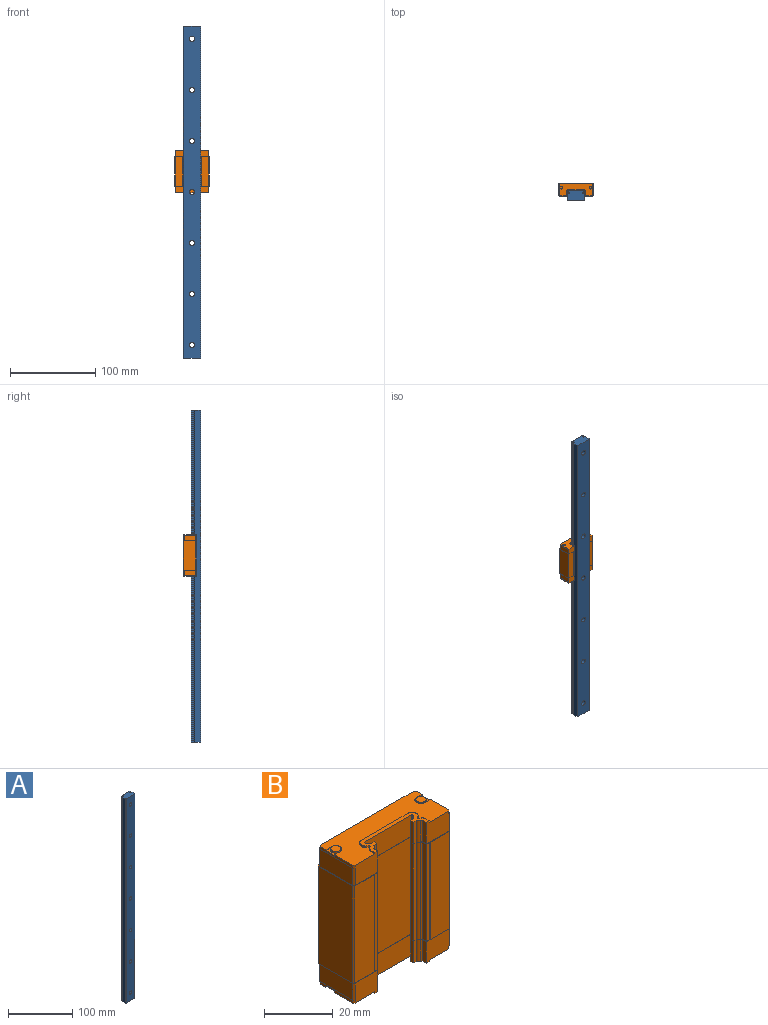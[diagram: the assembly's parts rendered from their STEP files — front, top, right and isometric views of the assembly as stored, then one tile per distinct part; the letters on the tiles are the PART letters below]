
ASSEMBLY  parts=2 mates=1
PART A: 47 faces, bbox 20x11x390 mm
  f0: plane 390x0.3mm, normal (-0.71,0.71,0), area 165.5mm2, adj f1,f2,f3,f27
  f1: plane 20x11mm, normal (0,0,1), area 210.1mm2, adj f0,f2,f3,f4,f5,f6,f7,f8
  f2: plane 390x19.4mm, normal (0,1,0), area 7069.8mm2, adj f0,f1,f24,f25,f27,f29,f32,f35
  f3: plane 390x0.48mm, normal (-1,0,0), area 185.7mm2, adj f0,f1,f4,f27
  f4: plane 390x0.56mm, normal (-0.5,-0.87,0), area 252.2mm2, adj f1,f3,f5,f27
  f5: cylinder r=1.75mm len=390mm, axis (0,0,1), area 427.5mm2, adj f1,f4,f6,f27
  f6: plane 390x1.22mm, normal (0,-1,0), area 474.9mm2, adj f1,f5,f7,f27
  f7: plane 390x1.2mm, normal (-1,0,0), area 468mm2, adj f1,f6,f8,f27
  f8: plane 390x1.22mm, normal (0,1,0), area 474.9mm2, adj f1,f7,f9,f27
  f9: cylinder r=1.75mm len=390mm, axis (0,0,1), area 427.5mm2, adj f1,f8,f10,f27
  f10: plane 390x0.56mm, normal (-0.5,0.87,0), area 252.2mm2, adj f1,f9,f11,f27
  f11: plane 390x6.28mm, normal (-1,0,0), area 2447.7mm2, adj f1,f10,f12,f27
  f12: plane 390x0.5mm, normal (-0.71,-0.71,0), area 275.8mm2, adj f1,f11,f13,f27
  f13: plane 390x19mm, normal (0,-1,0), area 7212.1mm2, adj f1,f12,f14,f27,f28,f31,f34,f37
  f14: plane 390x0.5mm, normal (0.71,-0.71,0), area 275.8mm2, adj f1,f13,f15,f27
  f15: plane 390x6.28mm, normal (1,0,0), area 2447.7mm2, adj f1,f14,f16,f27
  f16: plane 390x0.56mm, normal (0.5,0.87,0), area 252.2mm2, adj f1,f15,f17,f27
  f17: cylinder r=1.75mm len=390mm, axis (0,0,1), area 427.5mm2, adj f1,f16,f18,f27
  f18: plane 390x1.22mm, normal (0,1,0), area 474.9mm2, adj f1,f17,f19,f27
  f19: plane 390x1.2mm, normal (1,0,0), area 468mm2, adj f1,f18,f20,f27
  f20: plane 390x1.22mm, normal (0,-1,0), area 474.9mm2, adj f1,f19,f21,f27
  f21: cylinder r=1.75mm len=390mm, axis (0,0,1), area 427.5mm2, adj f1,f20,f22,f27
  f22: plane 390x0.56mm, normal (0.5,-0.87,0), area 252.2mm2, adj f1,f21,f23,f27
  f23: plane 390x0.48mm, normal (1,0,0), area 185.7mm2, adj f1,f22,f24,f27
  f24: plane 390x0.3mm, normal (0.71,0.71,0), area 165.5mm2, adj f1,f2,f23,f27
  f25: cylinder r=4.75mm len=9.5mm, axis (0,1,0), area 164.1mm2, adj f2,f26
  f26: plane 9.5x9.5mm, normal (0,1,0), area 42.6mm2, adj f25,f28
  f27: plane 20x11mm, normal (0,0,-1), area 210.1mm2, adj f0,f2,f3,f4,f5,f6,f7,f8
  f28: cylinder r=3mm len=6mm, axis (0,1,0), area 103.7mm2, adj f13,f26
  f29: cylinder r=4.75mm len=9.5mm, axis (0,1,0), area 164.1mm2, adj f2,f30
  f30: plane 9.5x9.5mm, normal (0,1,0), area 42.6mm2, adj f29,f31
  f31: cylinder r=3mm len=6mm, axis (0,1,0), area 103.7mm2, adj f13,f30
  f32: cylinder r=4.75mm len=9.5mm, axis (0,1,0), area 164.1mm2, adj f2,f33
  f33: plane 9.5x9.5mm, normal (0,1,0), area 42.6mm2, adj f32,f34
  f34: cylinder r=3mm len=6mm, axis (0,1,0), area 103.7mm2, adj f13,f33
  f35: cylinder r=4.75mm len=9.5mm, axis (0,1,0), area 164.1mm2, adj f2,f36
  f36: plane 9.5x9.5mm, normal (0,1,0), area 42.6mm2, adj f35,f37
  f37: cylinder r=3mm len=6mm, axis (0,1,0), area 103.7mm2, adj f13,f36
  f38: cylinder r=4.75mm len=9.5mm, axis (0,1,0), area 164.1mm2, adj f2,f39
  f39: plane 9.5x9.5mm, normal (0,1,0), area 42.6mm2, adj f38,f40
  f40: cylinder r=3mm len=6mm, axis (0,1,0), area 103.7mm2, adj f13,f39
  f41: cylinder r=4.75mm len=9.5mm, axis (0,1,0), area 164.1mm2, adj f2,f42
  f42: plane 9.5x9.5mm, normal (0,1,0), area 42.6mm2, adj f41,f43
  f43: cylinder r=3mm len=6mm, axis (0,1,0), area 103.7mm2, adj f13,f42
  f44: cylinder r=4.75mm len=9.5mm, axis (0,1,0), area 164.1mm2, adj f2,f45
  f45: plane 9.5x9.5mm, normal (0,1,0), area 42.6mm2, adj f44,f46
  f46: cylinder r=3mm len=6mm, axis (0,1,0), area 103.7mm2, adj f13,f45
PART B: 250 faces, bbox 40x15x50 mm
  f0: cone r=1.62mm half-angle=60deg, axis (0,1,0), area 9.5mm2, adj f107
  f1: plane 1x0.5mm, normal (0.71,-0.71,0), area 0.7mm2, adj f3,f6,f148,f215
  f2: plane 1x0.5mm, normal (-0.71,-0.71,0), area 0.7mm2, adj f9,f143,f148,f215
  f3: plane 7.4x1mm, normal (1,0,0), area 7.4mm2, adj f1,f148,f215,f222
  f4: plane 9.3x7.65mm, normal (0,-1,0), area 67.1mm2, adj f30,f96,f112,f146,f166,f175,f180,f181
  f5: plane 9.3x7.65mm, normal (0,-1,0), area 67.1mm2, adj f13,f29,f96,f146,f166,f174,f180,f197
  f6: plane 9.3x7.65mm, normal (0,-1,0), area 67.1mm2, adj f1,f7,f31,f49,f117,f148,f165,f215
  f7: plane 22.46x7.13mm, normal (0,0,1), area 47mm2, adj f6,f9,f17,f22,f23,f24,f31,f32
  f8: plane 34.6x0.3mm, normal (0.71,-0.71,0), area 14.7mm2, adj f26,f121,f122,f226
  f9: plane 9.3x7.65mm, normal (0,-1,0), area 67.1mm2, adj f2,f7,f32,f49,f118,f148,f149,f215
  f10: plane 34.6x1.68mm, normal (1,0,0), area 58mm2, adj f12,f121,f122,f244
  f11: plane 34.6x1.26mm, normal (0,-1,0), area 43.5mm2, adj f27,f121,f122,f136
  f12: plane 34.6x1.26mm, normal (0,-1,0), area 43.5mm2, adj f10,f121,f122,f137
  f13: plane 6.2x0.5mm, normal (0.71,-0.71,0), area 4.4mm2, adj f5,f73,f96,f109,f122,f166
  f14: plane 34.6x1.22mm, normal (0,1,0), area 42.1mm2, adj f15,f16,f121,f122
  f15: plane 34.6x1.2mm, normal (1,0,0), area 41.5mm2, adj f14,f121,f122,f249
  f16: cylinder r=1.75mm len=34.6mm, axis (0,0,1), area 37.9mm2, adj f14,f25,f121,f122
  f17: plane 7.65x1.22mm, normal (0,1,0), area 9.3mm2, adj f7,f22,f37,f49
  f18: plane 7.65x1.22mm, normal (0,1,0), area 9.3mm2, adj f19,f20,f96,f146
  f19: plane 7.65x1.2mm, normal (1,0,0), area 9.2mm2, adj f18,f96,f146,f248
  f20: cylinder r=1.75mm len=7.65mm, axis (0,0,1), area 8.4mm2, adj f18,f21,f96,f146
  f21: plane 7.65x0.56mm, normal (0.5,0.87,0), area 4.9mm2, adj f20,f28,f96,f146
  f22: cylinder r=1.75mm len=7.65mm, axis (0,0,1), area 8.4mm2, adj f7,f17,f23,f49
  f23: plane 7.65x0.56mm, normal (0.5,0.87,0), area 4.9mm2, adj f7,f22,f24,f49
  f24: plane 7.65x0.48mm, normal (1,0,0), area 3.6mm2, adj f7,f23,f48,f49
  f25: plane 34.6x0.56mm, normal (0.5,0.87,0), area 22.4mm2, adj f16,f26,f121,f122
  f26: plane 34.6x0.48mm, normal (1,0,0), area 16.5mm2, adj f8,f25,f121,f122
  f27: plane 34.6x1.68mm, normal (-1,0,0), area 58mm2, adj f11,f121,f122,f243
  f28: plane 7.65x0.48mm, normal (1,0,0), area 3.6mm2, adj f21,f96,f146,f223
  f29: plane 7.65x1.68mm, normal (-1,0,0), area 12.8mm2, adj f5,f96,f146,f241
  f30: plane 7.65x1.68mm, normal (1,0,0), area 12.8mm2, adj f4,f96,f146,f246
  f31: plane 7.65x1.68mm, normal (-1,0,0), area 12.8mm2, adj f6,f7,f38,f49
  f32: plane 7.65x1.68mm, normal (1,0,0), area 12.8mm2, adj f7,f9,f34,f49
  f33: plane 3x3mm, normal (0,0,-1), area 7.1mm2, adj f212
  f34: plane 7.65x0.56mm, normal (0.5,-0.87,0), area 4.9mm2, adj f7,f32,f35,f49
  f35: cylinder r=1.75mm len=7.65mm, axis (0,0,1), area 8.4mm2, adj f7,f34,f36,f49
  f36: plane 7.65x1.22mm, normal (0,-1,0), area 9.3mm2, adj f7,f35,f37,f49
  f37: plane 7.65x1.2mm, normal (1,0,0), area 9.2mm2, adj f7,f17,f36,f49
  f38: plane 7.65x0.56mm, normal (-0.5,-0.87,0), area 4.9mm2, adj f7,f31,f39,f49
  f39: cylinder r=1.75mm len=7.65mm, axis (0,0,1), area 8.4mm2, adj f7,f38,f40,f49
  f40: plane 7.65x1.22mm, normal (0,-1,0), area 9.3mm2, adj f7,f39,f41,f49
  f41: plane 7.65x1.2mm, normal (-1,0,0), area 9.2mm2, adj f7,f40,f42,f49
  f42: plane 7.65x1.22mm, normal (0,1,0), area 9.3mm2, adj f7,f41,f43,f49
  f43: cylinder r=1.75mm len=7.65mm, axis (0,0,1), area 8.4mm2, adj f7,f42,f44,f49
  f44: plane 7.65x0.56mm, normal (-0.5,0.87,0), area 4.9mm2, adj f7,f43,f45,f49
  f45: plane 7.65x0.48mm, normal (-1,0,0), area 3.6mm2, adj f7,f44,f46,f49
  f46: plane 7.65x0.3mm, normal (-0.71,-0.71,0), area 3.2mm2, adj f7,f45,f47,f49
  f47: plane 19.4x7.65mm, normal (0,-1,0), area 148.4mm2, adj f7,f46,f48,f49
  f48: plane 7.65x0.3mm, normal (0.71,-0.71,0), area 3.2mm2, adj f7,f24,f47,f49
  f49: plane 38.7x5.95mm, normal (0,0,-1), area 2.9mm2, adj f6,f9,f17,f22,f23,f24,f31,f32
  f50: plane 9.3x0.05mm, normal (0,-1,0), area 0.5mm2, adj f49,f51,f117,f121
  f51: plane 1.68x0.05mm, normal (-1,0,0), area 0.1mm2, adj f49,f50,f52,f121
  f52: plane 0.54x0.29mm, normal (-0.48,-0.88,0), area 0mm2, adj f49,f51,f53,f121
  f53: cylinder r=1.7mm len=0.83mm, axis (0,0,1), area 0.1mm2, adj f49,f52,f54,f121
  f54: plane 1.2x0.05mm, normal (0,-1,0), area 0.1mm2, adj f49,f53,f55,f121
  f55: plane 1.1x0.05mm, normal (-1,0,0), area 0.1mm2, adj f49,f54,f56,f121
  f56: plane 1.2x0.05mm, normal (0,1,0), area 0.1mm2, adj f49,f55,f57,f121
  f57: cylinder r=1.7mm len=0.83mm, axis (0,0,1), area 0.1mm2, adj f49,f56,f58,f121
  f58: plane 0.54x0.29mm, normal (-0.48,0.88,0), area 0mm2, adj f49,f57,f59,f121
  f59: plane 0.58x0.05mm, normal (-1,0,0), area 0mm2, adj f49,f58,f60,f121
  f60: plane 0.3x0.3mm, normal (-0.71,-0.71,0), area 0mm2, adj f49,f59,f61,f121
  f61: plane 19.5x0.05mm, normal (0,-1,0), area 1mm2, adj f49,f60,f62,f121
  f62: plane 0.3x0.3mm, normal (0.71,-0.71,0), area 0mm2, adj f49,f61,f63,f121
  f63: plane 0.58x0.05mm, normal (1,0,0), area 0mm2, adj f49,f62,f64,f121
  f64: plane 0.54x0.29mm, normal (0.48,0.88,0), area 0mm2, adj f49,f63,f65,f121
  f65: cylinder r=1.7mm len=0.83mm, axis (0,0,1), area 0.1mm2, adj f49,f64,f66,f121
  f66: plane 1.2x0.05mm, normal (0,1,0), area 0.1mm2, adj f49,f65,f67,f121
  f67: plane 1.1x0.05mm, normal (1,0,0), area 0.1mm2, adj f49,f66,f68,f121
  f68: plane 1.2x0.05mm, normal (0,-1,0), area 0.1mm2, adj f49,f67,f69,f121
  f69: cylinder r=1.7mm len=0.83mm, axis (0,0,1), area 0.1mm2, adj f49,f68,f70,f121
  f70: plane 0.54x0.29mm, normal (0.48,-0.88,0), area 0mm2, adj f49,f69,f71,f121
  f71: plane 1.68x0.05mm, normal (1,0,0), area 0.1mm2, adj f49,f70,f72,f121
  f72: plane 9.3x0.05mm, normal (0,-1,0), area 0.5mm2, adj f49,f71,f118,f121
  f73: plane 9.3x0.05mm, normal (0,-1,0), area 0.5mm2, adj f13,f74,f96,f122
  f74: plane 1.68x0.05mm, normal (-1,0,0), area 0.1mm2, adj f73,f75,f96,f122
  f75: plane 0.54x0.29mm, normal (-0.48,-0.88,0), area 0mm2, adj f74,f76,f96,f122
  f76: cylinder r=1.7mm len=0.83mm, axis (0,0,-1), area 0.1mm2, adj f75,f77,f96,f122
  f77: plane 1.2x0.05mm, normal (0,-1,0), area 0.1mm2, adj f76,f78,f96,f122
  f78: plane 1.1x0.05mm, normal (-1,0,0), area 0.1mm2, adj f77,f79,f96,f122
  f79: plane 1.2x0.05mm, normal (0,1,0), area 0.1mm2, adj f78,f80,f96,f122
  f80: cylinder r=1.7mm len=0.83mm, axis (0,0,-1), area 0.1mm2, adj f79,f81,f96,f122
  f81: plane 0.54x0.29mm, normal (-0.48,0.88,0), area 0mm2, adj f80,f82,f96,f122
  f82: plane 0.58x0.05mm, normal (-1,0,0), area 0mm2, adj f81,f83,f96,f122
  f83: plane 0.3x0.3mm, normal (-0.71,-0.71,0), area 0mm2, adj f82,f84,f96,f122
  f84: plane 19.5x0.05mm, normal (0,-1,0), area 1mm2, adj f83,f85,f96,f122
  f85: plane 0.3x0.3mm, normal (0.71,-0.71,0), area 0mm2, adj f84,f86,f96,f122
  f86: plane 0.58x0.05mm, normal (1,0,0), area 0mm2, adj f85,f87,f96,f122
  f87: plane 0.54x0.29mm, normal (0.48,0.88,0), area 0mm2, adj f86,f88,f96,f122
  f88: cylinder r=1.7mm len=0.83mm, axis (0,0,-1), area 0.1mm2, adj f87,f89,f96,f122
  f89: plane 1.2x0.05mm, normal (0,1,0), area 0.1mm2, adj f88,f90,f96,f122
  f90: plane 1.1x0.05mm, normal (1,0,0), area 0.1mm2, adj f89,f91,f96,f122
  f91: plane 1.2x0.05mm, normal (0,-1,0), area 0.1mm2, adj f90,f92,f96,f122
  f92: cylinder r=1.7mm len=0.83mm, axis (0,0,-1), area 0.1mm2, adj f91,f93,f96,f122
  f93: plane 0.54x0.29mm, normal (0.48,-0.88,0), area 0mm2, adj f92,f94,f96,f122
  f94: plane 1.68x0.05mm, normal (1,0,0), area 0.1mm2, adj f93,f95,f96,f122
  f95: plane 9.3x0.05mm, normal (0,-1,0), area 0.5mm2, adj f94,f96,f112,f122
  f96: plane 38.7x5.95mm, normal (0,0,1), area 2.9mm2, adj f4,f5,f13,f18,f19,f20,f21,f28
  f97: cone r=2mm half-angle=45deg, axis (0,1,0), area 6.1mm2, adj f98,f124
  f98: cylinder r=1.62mm len=7.62mm, axis (0,1,0), area 77.6mm2, adj f97,f99
  f99: cone r=1.62mm half-angle=60deg, axis (0,1,0), area 9.5mm2, adj f98
  f100: cone r=2mm half-angle=45deg, axis (0,1,0), area 6.1mm2, adj f101,f108
  f101: cylinder r=1.62mm len=7.62mm, axis (0,1,0), area 77.6mm2, adj f100,f102
  f102: cone r=1.62mm half-angle=60deg, axis (0,1,0), area 9.5mm2, adj f101
  f103: cone r=2mm half-angle=45deg, axis (0,1,0), area 6.1mm2, adj f104,f124
  f104: cylinder r=1.62mm len=7.62mm, axis (0,1,0), area 77.6mm2, adj f103,f105
  f105: cone r=1.62mm half-angle=60deg, axis (0,1,0), area 9.5mm2, adj f104
  f106: cone r=2mm half-angle=45deg, axis (0,1,0), area 6.1mm2, adj f107,f108
  f107: cylinder r=1.62mm len=7.62mm, axis (0,1,0), area 77.6mm2, adj f0,f106
  f108: plane 34.6x11.7mm, normal (0,1,0), area 379.7mm2, adj f100,f106,f121,f122,f131,f132
  f109: plane 13.4x6.2mm, normal (1,0,0), area 83.1mm2, adj f13,f110,f122,f166
  f110: plane 6.2x0.5mm, normal (0.71,0.71,0), area 4.4mm2, adj f109,f122,f147,f166
  f111: plane 13.4x6.2mm, normal (-1,0,0), area 83.1mm2, adj f112,f113,f122,f166
  f112: plane 6.2x0.5mm, normal (-0.71,-0.71,0), area 4.4mm2, adj f4,f95,f96,f111,f122,f166
  f113: plane 6.2x0.5mm, normal (-0.71,0.71,0), area 4.4mm2, adj f111,f122,f147,f166
  f114: plane 38.6x6.2mm, normal (0,1,0), area 239.3mm2, adj f115,f120,f121,f215
  f115: plane 6.2x0.5mm, normal (0.71,0.71,0), area 4.4mm2, adj f114,f116,f121,f215
  f116: plane 13.4x6.2mm, normal (1,0,0), area 83.1mm2, adj f115,f117,f121,f215
  f117: plane 6.2x0.5mm, normal (0.71,-0.71,0), area 4.4mm2, adj f6,f49,f50,f116,f121,f215
  f118: plane 6.2x0.5mm, normal (-0.71,-0.71,0), area 4.4mm2, adj f9,f49,f72,f119,f121,f215
  f119: plane 13.4x6.2mm, normal (-1,0,0), area 83.1mm2, adj f118,f120,f121,f215
  f120: plane 6.2x0.5mm, normal (-0.71,0.71,0), area 4.4mm2, adj f114,f119,f121,f215
  f121: plane 40x15mm, normal (0,0,1), area 26.7mm2, adj f8,f10,f11,f12,f14,f15,f16,f25
  f122: plane 40x15mm, normal (0,0,-1), area 26.7mm2, adj f8,f10,f11,f12,f13,f14,f15,f16
  f123: plane 34.6x0.5mm, normal (-0.71,0.71,0), area 24.5mm2, adj f121,f122,f124,f140
  f124: plane 34.6x11.7mm, normal (0,1,0), area 379.7mm2, adj f97,f103,f121,f122,f123,f125
  f125: plane 34.6x0.5mm, normal (0.67,0.74,0), area 23.3mm2, adj f121,f122,f124,f126
  f126: plane 34.6x3.6mm, normal (0,1,0), area 124.6mm2, adj f121,f122,f125,f127
  f127: plane 34.6x0.5mm, normal (-0.67,0.74,0), area 23.3mm2, adj f121,f122,f126,f128
  f128: plane 34.6x6.4mm, normal (0,1,0), area 221.4mm2, adj f121,f122,f127,f129
  f129: plane 34.6x0.5mm, normal (0.67,0.74,0), area 23.3mm2, adj f121,f122,f128,f130
  f130: plane 34.6x3.6mm, normal (0,1,0), area 124.6mm2, adj f121,f122,f129,f131
  f131: plane 34.6x0.5mm, normal (-0.67,0.74,0), area 23.3mm2, adj f108,f121,f122,f130
  f132: plane 34.6x0.5mm, normal (0.71,0.71,0), area 24.5mm2, adj f108,f121,f122,f133
  f133: plane 34.6x14mm, normal (1,0,0), area 484.4mm2, adj f121,f122,f132,f134
  f134: plane 34.6x0.5mm, normal (0.71,-0.71,0), area 24.5mm2, adj f121,f122,f133,f135
  f135: plane 34.6x8.03mm, normal (0,-1,0), area 277.8mm2, adj f121,f122,f134,f136
  f136: plane 34.6x0.21mm, normal (-0.42,-0.91,0), area 8.2mm2, adj f11,f121,f122,f135
  f137: plane 34.6x0.21mm, normal (0.42,-0.91,0), area 8.2mm2, adj f12,f121,f122,f138
  f138: plane 34.6x8.03mm, normal (0,-1,0), area 277.8mm2, adj f121,f122,f137,f139
  f139: plane 34.6x0.5mm, normal (-0.71,-0.71,0), area 24.5mm2, adj f121,f122,f138,f140
  f140: plane 34.6x14mm, normal (-1,0,0), area 484.4mm2, adj f121,f122,f123,f139
  f141: plane 2.3x1mm, normal (-1,0,0), area 2.3mm2, adj f145,f148,f215,f216
  f142: cylinder r=1.8mm len=3.6mm, axis (0,0,-1), area 2.3mm2, adj f144,f145,f148,f199
  f143: plane 7.4x1mm, normal (-1,0,0), area 7.4mm2, adj f2,f144,f148,f215
  f144: plane 2.25x1mm, normal (0,1,0), area 1mm2, adj f142,f143,f148,f198,f199,f215
  f145: plane 2.25x1mm, normal (0,-1,0), area 1mm2, adj f141,f142,f148,f198,f199,f215
  f146: plane 22.46x7.13mm, normal (0,0,-1), area 47mm2, adj f4,f5,f18,f19,f20,f21,f28,f29
  f147: plane 38.6x6.2mm, normal (0,1,0), area 239.3mm2, adj f110,f113,f122,f166
  f148: plane 39.5x14.3mm, normal (0,0,1), area 382.6mm2, adj f1,f2,f3,f6,f9,f141,f142,f143
  f149: plane 1.64x0.5mm, normal (-1,0,0), area 0.8mm2, adj f7,f9,f148,f150
  f150: cylinder r=1.3mm len=1.13mm, axis (0,0,-1), area 0.7mm2, adj f7,f148,f149,f151
  f151: plane 0.51x0.5mm, normal (-0.5,0.87,0), area 0.3mm2, adj f7,f148,f150,f152
  f152: cylinder r=0.4mm len=0.69mm, axis (0,0,-1), area 0.4mm2, adj f7,f148,f151,f153
  f153: plane 0.51x0.5mm, normal (-0.5,-0.87,0), area 0.3mm2, adj f7,f148,f152,f154
  f154: cylinder r=1.3mm len=1.13mm, axis (0,0,-1), area 0.7mm2, adj f7,f148,f153,f155
  f155: plane 0.5x0.37mm, normal (-1,0,0), area 0.2mm2, adj f7,f148,f154,f156
  f156: cylinder r=1.6mm len=1.6mm, axis (0,0,-1), area 1.3mm2, adj f7,f148,f155,f157
  f157: plane 19.26x0.5mm, normal (0,1,0), area 9.6mm2, adj f7,f148,f156,f158
  f158: cylinder r=1.6mm len=1.6mm, axis (0,0,-1), area 1.3mm2, adj f7,f148,f157,f159
  f159: plane 0.5x0.37mm, normal (1,0,0), area 0.2mm2, adj f7,f148,f158,f160
  f160: cylinder r=1.3mm len=1.13mm, axis (0,0,-1), area 0.7mm2, adj f7,f148,f159,f161
  f161: plane 0.51x0.5mm, normal (0.5,-0.87,0), area 0.3mm2, adj f7,f148,f160,f162
  f162: cylinder r=0.4mm len=0.69mm, axis (0,0,-1), area 0.4mm2, adj f7,f148,f161,f163
  f163: plane 0.51x0.5mm, normal (0.5,0.87,0), area 0.3mm2, adj f7,f148,f162,f164
  f164: cylinder r=1.3mm len=1.13mm, axis (0,0,-1), area 0.7mm2, adj f7,f148,f163,f165
  f165: plane 1.64x0.5mm, normal (1,0,0), area 0.8mm2, adj f6,f7,f148,f164
  f166: plane 39.6x14.4mm, normal (0,0,-1), area 6.8mm2, adj f4,f5,f13,f109,f110,f111,f112,f113
  f167: plane 1x0.5mm, normal (-0.71,0.71,0), area 0.7mm2, adj f166,f168,f179,f180
  f168: plane 38.5x1mm, normal (0,1,0), area 38.5mm2, adj f166,f167,f169,f180
  f169: plane 1x0.5mm, normal (0.71,0.71,0), area 0.7mm2, adj f166,f168,f170,f180
  f170: plane 2.3x1mm, normal (1,0,0), area 2.3mm2, adj f166,f169,f171,f180
  f171: plane 2.25x1mm, normal (0,-1,0), area 1mm2, adj f166,f170,f180,f204,f205,f213
  f172: plane 2.25x1mm, normal (0,1,0), area 1mm2, adj f166,f173,f180,f204,f205,f213
  f173: plane 7.4x1mm, normal (1,0,0), area 7.4mm2, adj f166,f172,f174,f180
  f174: plane 1x0.5mm, normal (0.71,-0.71,0), area 0.7mm2, adj f5,f166,f173,f180
  f175: plane 1x0.5mm, normal (-0.71,-0.71,0), area 0.7mm2, adj f4,f166,f176,f180
  f176: plane 7.4x1mm, normal (-1,0,0), area 7.4mm2, adj f166,f175,f177,f180
  f177: plane 2.25x1mm, normal (0,1,0), area 1mm2, adj f166,f176,f180,f202,f203,f214
  f178: plane 2.25x1mm, normal (0,-1,0), area 1mm2, adj f166,f179,f180,f202,f203,f214
  f179: plane 2.3x1mm, normal (-1,0,0), area 2.3mm2, adj f166,f167,f178,f180
  f180: plane 39.5x14.3mm, normal (0,0,-1), area 382.6mm2, adj f4,f5,f167,f168,f169,f170,f171,f172
  f181: plane 1.64x0.5mm, normal (-1,0,0), area 0.8mm2, adj f4,f146,f180,f182
  f182: cylinder r=1.3mm len=1.13mm, axis (0,0,1), area 0.7mm2, adj f146,f180,f181,f183
  f183: plane 0.51x0.5mm, normal (-0.5,0.87,0), area 0.3mm2, adj f146,f180,f182,f184
  f184: cylinder r=0.4mm len=0.69mm, axis (0,0,1), area 0.4mm2, adj f146,f180,f183,f185
  f185: plane 0.51x0.5mm, normal (-0.5,-0.87,0), area 0.3mm2, adj f146,f180,f184,f186
  f186: cylinder r=1.3mm len=1.13mm, axis (0,0,1), area 0.7mm2, adj f146,f180,f185,f187
  f187: plane 0.5x0.37mm, normal (-1,0,0), area 0.2mm2, adj f146,f180,f186,f188
  f188: cylinder r=1.6mm len=1.6mm, axis (0,0,1), area 1.3mm2, adj f146,f180,f187,f189
  f189: plane 19.26x0.5mm, normal (0,1,0), area 9.6mm2, adj f146,f180,f188,f190
  f190: cylinder r=1.6mm len=1.6mm, axis (0,0,1), area 1.3mm2, adj f146,f180,f189,f191
  f191: plane 0.5x0.37mm, normal (1,0,0), area 0.2mm2, adj f146,f180,f190,f192
  f192: cylinder r=1.3mm len=1.13mm, axis (0,0,1), area 0.7mm2, adj f146,f180,f191,f193
  f193: plane 0.51x0.5mm, normal (0.5,-0.87,0), area 0.3mm2, adj f146,f180,f192,f194
  f194: cylinder r=0.4mm len=0.69mm, axis (0,0,1), area 0.4mm2, adj f146,f180,f193,f195
  f195: plane 0.51x0.5mm, normal (0.5,0.87,0), area 0.3mm2, adj f146,f180,f194,f196
  f196: cylinder r=1.3mm len=1.13mm, axis (0,0,1), area 0.7mm2, adj f146,f180,f195,f197
  f197: plane 1.64x0.5mm, normal (1,0,0), area 0.8mm2, adj f5,f146,f180,f196
  f198: plane 3.6x0.6mm, normal (-1,0,0), area 2.2mm2, adj f144,f145,f199,f215
  f199: plane 3.85x3.6mm, normal (0,0,1), area 5.4mm2, adj f142,f144,f145,f198,f207
  f200: plane 3.6x0.6mm, normal (1,0,0), area 2.2mm2, adj f201,f215,f220,f222
  f201: plane 3.85x3.6mm, normal (0,0,1), area 5.4mm2, adj f200,f211,f220,f221,f222
  f202: plane 3.6x0.6mm, normal (-1,0,0), area 2.2mm2, adj f166,f177,f178,f203
  f203: plane 3.85x3.6mm, normal (0,0,-1), area 5.4mm2, adj f177,f178,f202,f208,f214
  f204: plane 3.6x0.6mm, normal (1,0,0), area 2.2mm2, adj f166,f171,f172,f205
  f205: plane 3.85x3.6mm, normal (0,0,-1), area 5.4mm2, adj f171,f172,f204,f212,f213
  f206: plane 3x3mm, normal (0,0,1), area 7.1mm2, adj f207
  f207: cylinder r=1.5mm len=3mm, axis (0,0,1), area 5.7mm2, adj f199,f206
  f208: cylinder r=1.5mm len=3mm, axis (0,0,1), area 5.7mm2, adj f203,f209
  f209: plane 3x3mm, normal (0,0,-1), area 7.1mm2, adj f208
  f210: plane 3x3mm, normal (0,0,1), area 7.1mm2, adj f211
  f211: cylinder r=1.5mm len=3mm, axis (0,0,1), area 5.7mm2, adj f201,f210
  f212: cylinder r=1.5mm len=3mm, axis (0,0,1), area 5.7mm2, adj f33,f205
  f213: cylinder r=1.8mm len=3.6mm, axis (0,0,1), area 2.3mm2, adj f171,f172,f180,f205
  f214: cylinder r=1.8mm len=3.6mm, axis (0,0,1), area 2.3mm2, adj f177,f178,f180,f203
  f215: plane 39.6x14.4mm, normal (0,0,1), area 6.8mm2, adj f1,f2,f3,f6,f9,f114,f115,f116
  f216: plane 1x0.5mm, normal (-0.71,0.71,0), area 0.7mm2, adj f141,f148,f215,f217
  f217: plane 38.5x1mm, normal (0,1,0), area 38.5mm2, adj f148,f215,f216,f218
  f218: plane 1x0.5mm, normal (0.71,0.71,0), area 0.7mm2, adj f148,f215,f217,f219
  f219: plane 2.3x1mm, normal (1,0,0), area 2.3mm2, adj f148,f215,f218,f220
  f220: plane 2.25x1mm, normal (0,-1,0), area 1mm2, adj f148,f200,f201,f215,f219,f221
  f221: cylinder r=1.8mm len=3.6mm, axis (0,0,-1), area 2.3mm2, adj f148,f201,f220,f222
  f222: plane 2.25x1mm, normal (0,1,0), area 1mm2, adj f3,f148,f200,f201,f215,f221
  f223: plane 7.65x0.3mm, normal (0.71,-0.71,0), area 3.2mm2, adj f28,f96,f146,f224
  f224: plane 19.4x7.65mm, normal (0,-1,0), area 148.4mm2, adj f96,f146,f223,f225
  f225: plane 7.65x0.3mm, normal (-0.71,-0.71,0), area 3.2mm2, adj f96,f146,f224,f230
  f226: plane 34.6x19.4mm, normal (0,-1,0), area 671.2mm2, adj f8,f121,f122,f227
  f227: plane 34.6x0.3mm, normal (-0.71,-0.71,0), area 14.7mm2, adj f121,f122,f226,f228
  f228: plane 34.6x0.48mm, normal (-1,0,0), area 16.5mm2, adj f121,f122,f227,f229
  f229: plane 34.6x0.56mm, normal (-0.5,0.87,0), area 22.4mm2, adj f121,f122,f228,f234
  f230: plane 7.65x0.48mm, normal (-1,0,0), area 3.6mm2, adj f96,f146,f225,f231
  f231: plane 7.65x0.56mm, normal (-0.5,0.87,0), area 4.9mm2, adj f96,f146,f230,f232
  f232: cylinder r=1.75mm len=7.65mm, axis (0,0,1), area 8.4mm2, adj f96,f146,f231,f233
  f233: plane 7.65x1.22mm, normal (0,1,0), area 9.3mm2, adj f96,f146,f232,f238
  f234: cylinder r=1.75mm len=34.6mm, axis (0,0,1), area 37.9mm2, adj f121,f122,f229,f235
  f235: plane 34.6x1.22mm, normal (0,1,0), area 42.1mm2, adj f121,f122,f234,f236
  f236: plane 34.6x1.2mm, normal (-1,0,0), area 41.5mm2, adj f121,f122,f235,f237
  f237: plane 34.6x1.22mm, normal (0,-1,0), area 42.1mm2, adj f121,f122,f236,f242
  f238: plane 7.65x1.2mm, normal (-1,0,0), area 9.2mm2, adj f96,f146,f233,f239
  f239: plane 7.65x1.22mm, normal (0,-1,0), area 9.3mm2, adj f96,f146,f238,f240
  f240: cylinder r=1.75mm len=7.65mm, axis (0,0,1), area 8.4mm2, adj f96,f146,f239,f241
  f241: plane 7.65x0.56mm, normal (-0.5,-0.87,0), area 4.9mm2, adj f29,f96,f146,f240
  f242: cylinder r=1.75mm len=34.6mm, axis (0,0,1), area 37.9mm2, adj f121,f122,f237,f243
  f243: plane 34.6x0.56mm, normal (-0.5,-0.87,0), area 22.4mm2, adj f27,f121,f122,f242
  f244: plane 34.6x0.56mm, normal (0.5,-0.87,0), area 22.4mm2, adj f10,f121,f122,f245
  f245: cylinder r=1.75mm len=34.6mm, axis (0,0,1), area 37.9mm2, adj f121,f122,f244,f249
  f246: plane 7.65x0.56mm, normal (0.5,-0.87,0), area 4.9mm2, adj f30,f96,f146,f247
  f247: cylinder r=1.75mm len=7.65mm, axis (0,0,1), area 8.4mm2, adj f96,f146,f246,f248
  f248: plane 7.65x1.22mm, normal (0,-1,0), area 9.3mm2, adj f19,f96,f146,f247
  f249: plane 34.6x1.22mm, normal (0,-1,0), area 42.1mm2, adj f15,f121,f122,f245
PLACE A rot(axis=(0,0,1),0deg) t=(121.45,293.6,-654.94)mm
PLACE B t=(121.45,293.6,-630.8)mm
MATE slider A.f1 <-> B.f7  axis (0,0,1) through (121.45,304.6,-459.94)mm
